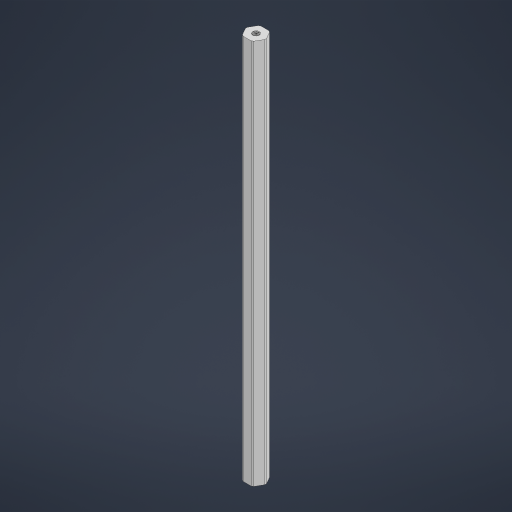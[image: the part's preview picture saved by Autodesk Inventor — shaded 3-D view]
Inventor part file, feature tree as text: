
AUTODESK INVENTOR PART (.ipt)
format: ipt  version: 2023 (Build 270158000, 158)  size: 756,224 bytes
history: native  units: in
note: dims shown in document units (in); Inventor stores cm internally (conversion verified against a paired STEP export)
features: mirror x1
ambient origin geometry x8: Origin, YZ Plane, XZ Plane, XY Plane, X Axis, Y Axis, Z Axis, Center Point
bodies: Solid1 (feature_tree)
feature tree (1):
  mirror  "Mirror2"
